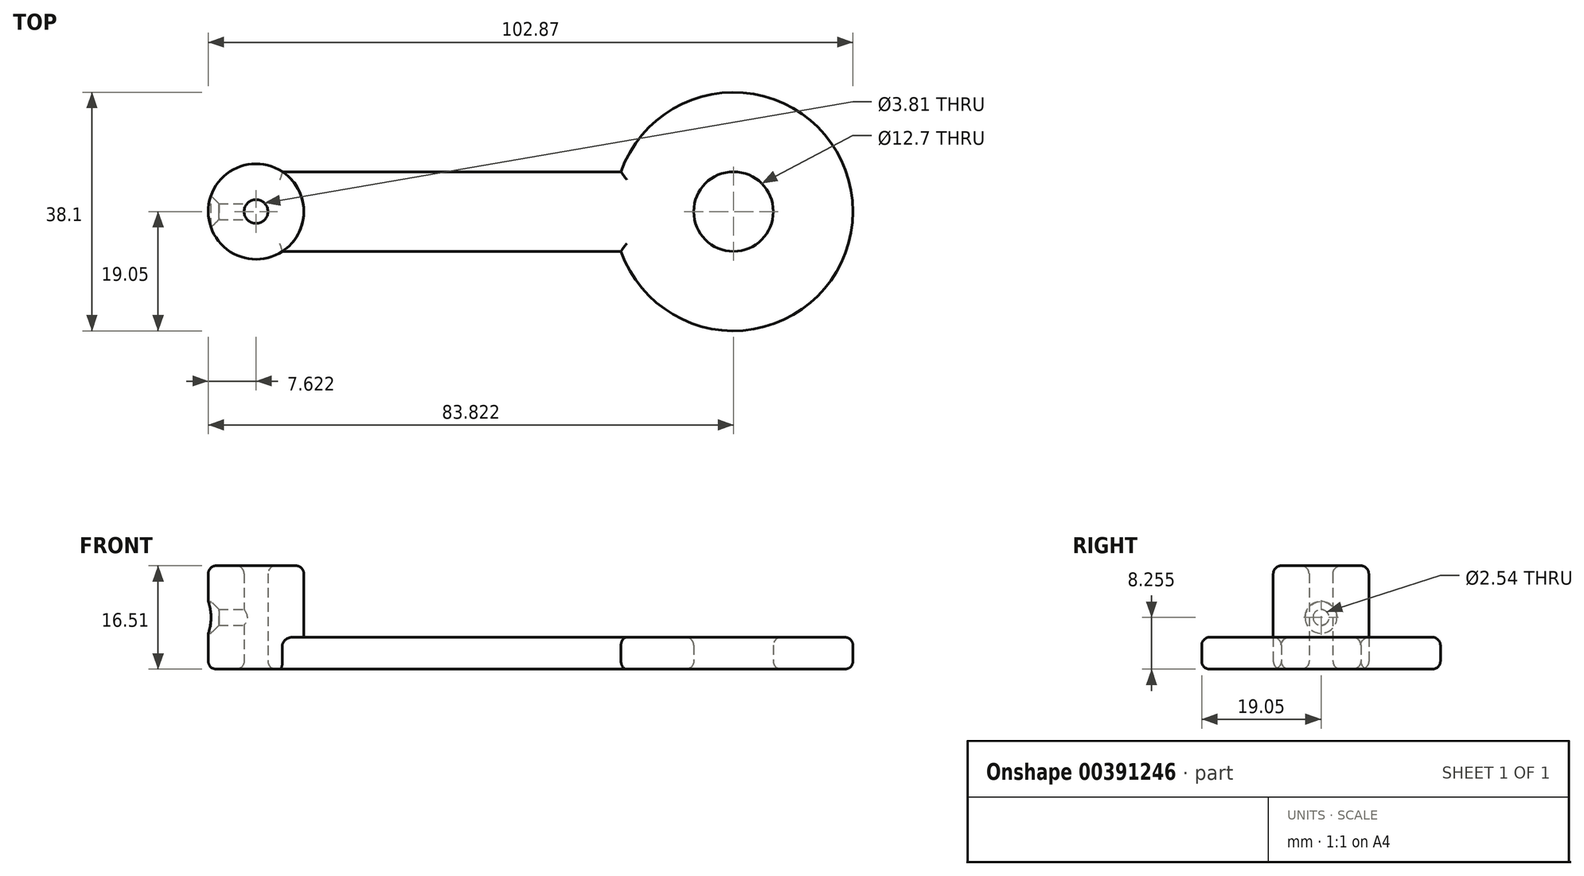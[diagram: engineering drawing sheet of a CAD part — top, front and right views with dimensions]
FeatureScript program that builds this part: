
annotation { "Feature Type Name" : "Feature", "Feature Type Description" : "" }
export const myFeature = defineFeature(function(context is Context, id is Id, definition is map)
    precondition{}
    {
        {
            var Q0;
            Q0=qCreatedBy(makeId("Top.planeOp"),FACE);
            var sketch = newSketch(context, id + "F0", { "sketchPlane" : qUnion([Q0])});
            skLineSegment(sketch, "E0.bottom", {"start": v(19.42, -6.35) * mm, "end": v(-34.6, -6.35) * mm});
            skLineSegment(sketch, "E0.top", {"start": v(19.42, 6.35) * mm, "end": v(-34.6, 6.35) * mm});
            skPoint(sketch, "E0.middle", {"position": v(0, 0) * mm});
            skArc(sketch, "E1", {"start": v(19.42, -6.35) * mm, "mid": v(56.43, 0) * mm, "end": v(19.42, 6.35) * mm});
            skArc(sketch, "E2", {"start": v(-34.6, 6.35) * mm, "mid": v(-46.44, 0) * mm, "end": v(-34.6, -6.35) * mm});
            skCircle(sketch, "E3", {"center": v(37.38, 0) * mm, "radius": 6.35 * mm});
            skCircle(sketch, "E4", {"center": v(-38.82, 0) * mm, "radius": 1.9 * mm});
            skSolve(sketch);
        }
        {
            var Q0;
            Q0=makeQuery(id+"F0.imprint","IMPRINT",FACE,{"disambiguationData":[TD([[makeQuery(id+"F0.imprint","IMPRINT",EDGE,{"derivedFrom":sQuery(id+"F0.wireOp",EDGE,"E0.bottom")}),-1.0]])]});
            extrude(context, id + "F1", {"entities" : qUnion([Q0]), "depth" : 5.08 * mm});
        }
        {
            var Q0;
            Q0=makeQuery(id+"F1.opExtrude","CAP_FACE",FACE,{"disambiguationData":[OSD([sQuery(id+"F0.wireOp",EDGE,"E0.bottom"),sQuery(id+"F0.wireOp",EDGE,"E0.top"),sQuery(id+"F0.wireOp",EDGE,"E1"),sQuery(id+"F0.wireOp",EDGE,"E2"),sQuery(id+"F0.wireOp",EDGE,"E3")])],"isStart":false});
            var Q1;
            Q1=makeQuery(id+"F1.opExtrude","CAP_FACE",FACE,{"disambiguationData":[OSD([sQuery(id+"F0.wireOp",EDGE,"E0.bottom"),sQuery(id+"F0.wireOp",EDGE,"E0.top"),sQuery(id+"F0.wireOp",EDGE,"E1"),sQuery(id+"F0.wireOp",EDGE,"E2"),sQuery(id+"F0.wireOp",EDGE,"E3")])],"isStart":true});
            fillet(context, id + "F2", {"entities" : qUnion([Q0, Q1]), "radius" : 1.27 * mm, "tangentPropagation" : true, "allowEdgeOverflow" : false});
        }
        {
            var Q0;
            {var subQ0=sQuery(id+"F0.wireOp",EDGE,"E2");Q0=makeQuery(id+"F2.opFillet","BLEND_EDGE",EDGE,{"blendedFrom":[makeQuery(id+"F1.opExtrude","CAP_EDGE",EDGE,{"disambiguationData":[OSD([subQ0])],"isStart":false}),makeQuery(id+"F1.opExtrude","SWEPT_FACE",FACE,{"disambiguationData":[OSD([subQ0])]})],"blendedInto":[makeQuery(id+"F1.opExtrude","SWEPT_FACE",FACE,{"disambiguationData":[OSD([subQ0])]})]});}
            cPoint(context, id + "F3", {"entities" : qUnion([Q0]), "parameter" : 0.5});
        }
        {
            var Q0;
            {var subQ0=sQuery(id+"F0.wireOp",EDGE,"E2");var subQ1=sQuery(id+"F0.wireOp",EDGE,"E0.bottom");Q0=makeQuery(id+"F2.opFillet","BLEND_VERTEX",VERTEX,{"blendedFrom":[makeQuery(id+"F1.opExtrude","CAP_EDGE",EDGE,{"disambiguationData":[OSD([subQ1])],"isStart":false}),makeQuery(id+"F1.opExtrude","CAP_EDGE",EDGE,{"disambiguationData":[OSD([subQ0])],"isStart":false}),makeQuery(id+"F1.opExtrude","SWEPT_FACE",FACE,{"disambiguationData":[OSD([subQ1])]}),makeQuery(id+"F1.opExtrude","SWEPT_FACE",FACE,{"disambiguationData":[OSD([subQ0])]})],"blendedInto":[makeQuery(id+"F1.opExtrude","SWEPT_FACE",FACE,{"disambiguationData":[OSD([subQ1])]}),makeQuery(id+"F1.opExtrude","SWEPT_FACE",FACE,{"disambiguationData":[OSD([subQ0])]})]});}
            var Q1;
            Q1 = qCreatedBy(id + "F3" ,VERTEX);
            var Q2;
            {var subQ0=sQuery(id+"F0.wireOp",EDGE,"E2");var subQ1=sQuery(id+"F0.wireOp",EDGE,"E0.top");Q2=makeQuery(id+"F2.opFillet","BLEND_VERTEX",VERTEX,{"blendedFrom":[makeQuery(id+"F1.opExtrude","CAP_EDGE",EDGE,{"disambiguationData":[OSD([subQ1])],"isStart":false}),makeQuery(id+"F1.opExtrude","CAP_EDGE",EDGE,{"disambiguationData":[OSD([subQ0])],"isStart":false}),makeQuery(id+"F1.opExtrude","SWEPT_FACE",FACE,{"disambiguationData":[OSD([subQ1])]}),makeQuery(id+"F1.opExtrude","SWEPT_FACE",FACE,{"disambiguationData":[OSD([subQ0])]})],"blendedInto":[makeQuery(id+"F1.opExtrude","SWEPT_FACE",FACE,{"disambiguationData":[OSD([subQ1])]}),makeQuery(id+"F1.opExtrude","SWEPT_FACE",FACE,{"disambiguationData":[OSD([subQ0])]})]});}
            cPlane(context, id + "F4", {"entities" : qUnion([Q0, Q1, Q2]), "cplaneType" : CPlaneType.THREE_POINT, "offset" : 25.4 * mm, "width" : 152.4 * mm, "height" : 152.4 * mm});
        }
        {
            var Q0;
            Q0=qCreatedBy(id+"F4.planeOp",FACE);
            var sketch = newSketch(context, id + "F5", { "sketchPlane" : qUnion([Q0])});
            skPoint(sketch, "E5.0", {"position": v(-38.82, 0) * mm});
            skArc(sketch, "E6.0", {"start": v(-34.6, 6.35) * mm, "mid": v(-46.44, 0) * mm, "end": v(-34.6, -6.35) * mm});
            skCircle(sketch, "E7", {"center": v(-38.82, 0) * mm, "radius": 7.62 * mm});
            skPoint(sketch, "E7.second.point", {"position": v(-46.44, 0) * mm});
            skCircle(sketch, "E8.0", {"center": v(-38.82, 0) * mm, "radius": 1.9 * mm});
            skPoint(sketch, "E9.first.point", {"position": v(-38.95, 1.9) * mm});
            skPoint(sketch, "E9.second.point", {"position": v(-37.25, -1.08) * mm});
            skPoint(sketch, "E9.third.point", {"position": v(-40.56, -0.78) * mm});
            skPoint(sketch, "E10", {"position": v(-38.95, 7.62) * mm});
            skPoint(sketch, "E11", {"position": v(-46.44, 7.62) * mm});
            skSolve(sketch);
        }
        {
            var Q0;
            Q0 = qSketchRegion(id + "F5", true);
            extrude(context, id + "F6", {"entities" : qUnion([Q0]), "operationType" : NewBodyOperationType.ADD, "depth" : 12.7 * mm});
        }
        {
            var Q0;
            Q0=makeQuery(id+"F6.opExtrude","CAP_EDGE",EDGE,{"disambiguationData":[OSD([sQuery(id+"F5.wireOp",EDGE,"E7")])],"isStart":false});
            var Q1;
            Q1=makeQuery(id+"F6.opExtrude","CAP_EDGE",EDGE,{"disambiguationData":[OSD([sQuery(id+"F5.wireOp",EDGE,"E8.0")])],"isStart":false});
            fillet(context, id + "F7", {"entities" : qUnion([Q0, Q1]), "radius" : 1.27 * mm, "tangentPropagation" : true, "allowEdgeOverflow" : false});
        }
        {
            var Q0;
            Q0=makeQuery(id+"F6.opExtrude","CAP_FACE",FACE,{"disambiguationData":[OSD([sQuery(id+"F5.wireOp",EDGE,"E7"),sQuery(id+"F5.wireOp",EDGE,"E8.0")])],"isStart":false});
            var sketch = newSketch(context, id + "F8", { "sketchPlane" : qUnion([Q0])});
            skPoint(sketch, "E12.0", {"position": v(-38.82, 0) * mm});
            skPoint(sketch, "E13", {"position": v(-38.82, -6.35) * mm});
            skSolve(sketch);
        }
        {
            var Q0;
            Q0=sQuery(id+"F8.wireOp",VERTEX,"E12.0");
            var Q1;
            Q1=sQuery(id+"F0.wireOp",VERTEX,"E4.center");
            var Q2;
            Q2=sQuery(id+"F8.wireOp",VERTEX,"E13");
            cPlane(context, id + "F9", {"entities" : qUnion([Q0, Q1, Q2]), "cplaneType" : CPlaneType.THREE_POINT, "offset" : 25.4 * mm, "width" : 152.4 * mm, "height" : 152.4 * mm});
        }
        {
            var Q0;
            Q0=qCreatedBy(id+"F9.planeOp",FACE);
            var sketch = newSketch(context, id + "F10", { "sketchPlane" : qUnion([Q0])});
            skLineSegment(sketch, "E14", {"start": v(-7.62, 1.27) * mm, "end": v(-7.62, 15.24) * mm});
            skLineSegment(sketch, "E15", {"start": v(7.62, 15.24) * mm, "end": v(7.62, 1.27) * mm});
            skPoint(sketch, "E16", {"position": v(7.62, 8.26) * mm});
            skPoint(sketch, "E17", {"position": v(0, 8.26) * mm});
            skSolve(sketch);
        }
        {
            var Q0;
            {var subQ0=sQuery(id+"F5.wireOp",EDGE,"E8.0");var subQ1=sQuery(id+"F5.wireOp",EDGE,"E7");var subQ2=makeQuery(id+"F6.opExtrude","CAP_FACE",FACE,{"disambiguationData":[OSD([subQ1,subQ0])],"isStart":false});Q0=makeQuery(id+"F8.imprint","IMPRINT",FACE,{"disambiguationData":[TD([[makeQuery(id+"F8.imprint","IMPRINT",EDGE,{"derivedFrom":makeQuery(id+"F7.opFillet","BLEND_EDGE",EDGE,{"blendedFrom":[makeQuery(id+"F6.opExtrude","CAP_EDGE",EDGE,{"disambiguationData":[OSD([subQ1])],"isStart":false}),subQ2],"blendedInto":[subQ2]})}),1.0]])]});}
            var sketch = newSketch(context, id + "F11", { "sketchPlane" : qUnion([Q0])});
            skPoint(sketch, "E18.0", {"position": v(-46.44, 0) * mm});
            skSolve(sketch);
        }
        {
            var Q0;
            Q0=sQuery(id+"F5.wireOp",VERTEX,"E11");
            var Q1;
            Q1=sQuery(id+"F5.wireOp",VERTEX,"E7.second.point");
            var Q2;
            Q2=sQuery(id+"F11.wireOp",VERTEX,"E18.0");
            cPlane(context, id + "F12", {"entities" : qUnion([Q0, Q1, Q2]), "cplaneType" : CPlaneType.THREE_POINT, "offset" : 25.4 * mm, "width" : 152.4 * mm, "height" : 152.4 * mm});
        }
        {
            var Q0;
            Q0=qCreatedBy(id+"F12.planeOp",FACE);
            var sketch = newSketch(context, id + "F13", { "sketchPlane" : qUnion([Q0])});
            skPoint(sketch, "E19.0", {"position": v(0, 8.26) * mm});
            skSolve(sketch);
        }
        {
            var Q0;
            Q0=sQuery(id+"F13.wireOp",VERTEX,"E19.0");
            var Q1;
            Q1=makeQuery(id+"F1.opExtrude","SWEPT_BODY",BODY,{"disambiguationData":[OSD([sQuery(id+"F0.wireOp",EDGE,"E0.bottom"),sQuery(id+"F0.wireOp",EDGE,"E0.top"),sQuery(id+"F0.wireOp",EDGE,"E1"),sQuery(id+"F0.wireOp",EDGE,"E2"),sQuery(id+"F0.wireOp",EDGE,"E3"),sQuery(id+"F0.wireOp",EDGE,"E4")])]});
            hole(context, id + "F14", {"style" : HoleStyle.C_SINK, "endStyle" : HoleEndStyle.BLIND, "oppositeDirection" : true, "holeDiameter" : 2.54 * mm, "cSinkDiameter" : 5.08 * mm, "cSinkAngle" : 90 * degree, "holeDepth" : 6.35 * mm, "isTappedThrough" : true, "tappedDepth" : 12.7 * mm, "tapClearance" : 3, "locations" : qUnion([Q0]), "scope" : qUnion([Q1])});
        }
    });
